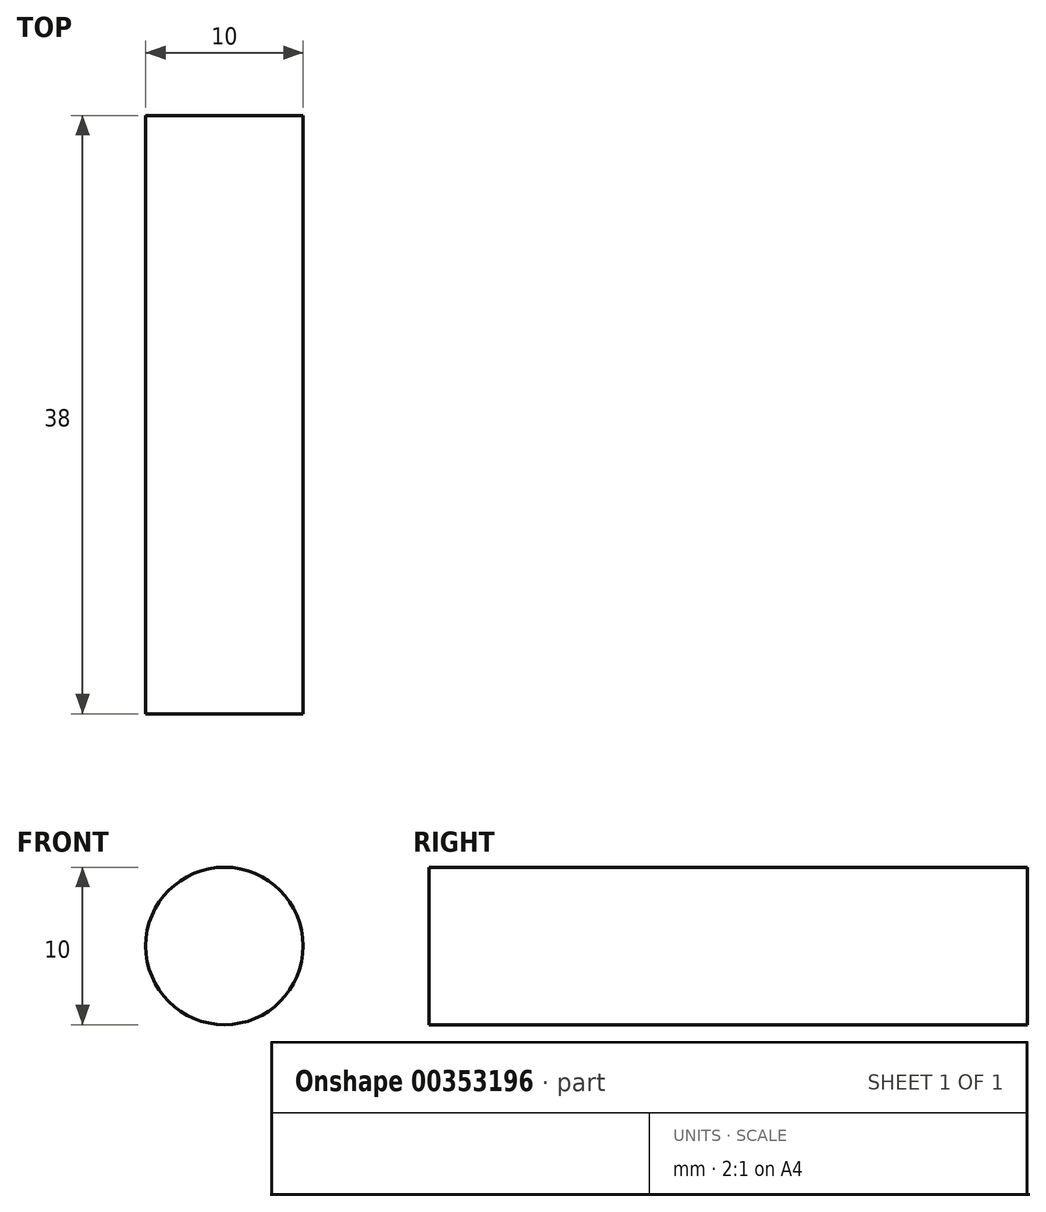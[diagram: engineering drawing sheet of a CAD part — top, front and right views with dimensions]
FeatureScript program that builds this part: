
annotation { "Feature Type Name" : "Feature", "Feature Type Description" : "" }
export const myFeature = defineFeature(function(context is Context, id is Id, definition is map)
    precondition{}
    {
        {
            var Q0;
            Q0=qCreatedBy(makeId("Front.planeOp"),FACE);
            var sketch = newSketch(context, id + "F0", { "sketchPlane" : qUnion([Q0])});
            skCircle(sketch, "E0", {"center": v(0, 0) * mm, "radius": 5 * mm});
            skSolve(sketch);
        }
        {
            var Q0;
            Q0 = qSketchRegion(id + "F0", true);
            extrude(context, id + "F1", {"entities" : qUnion([Q0]), "depth" : 38 * mm});
        }
    });
